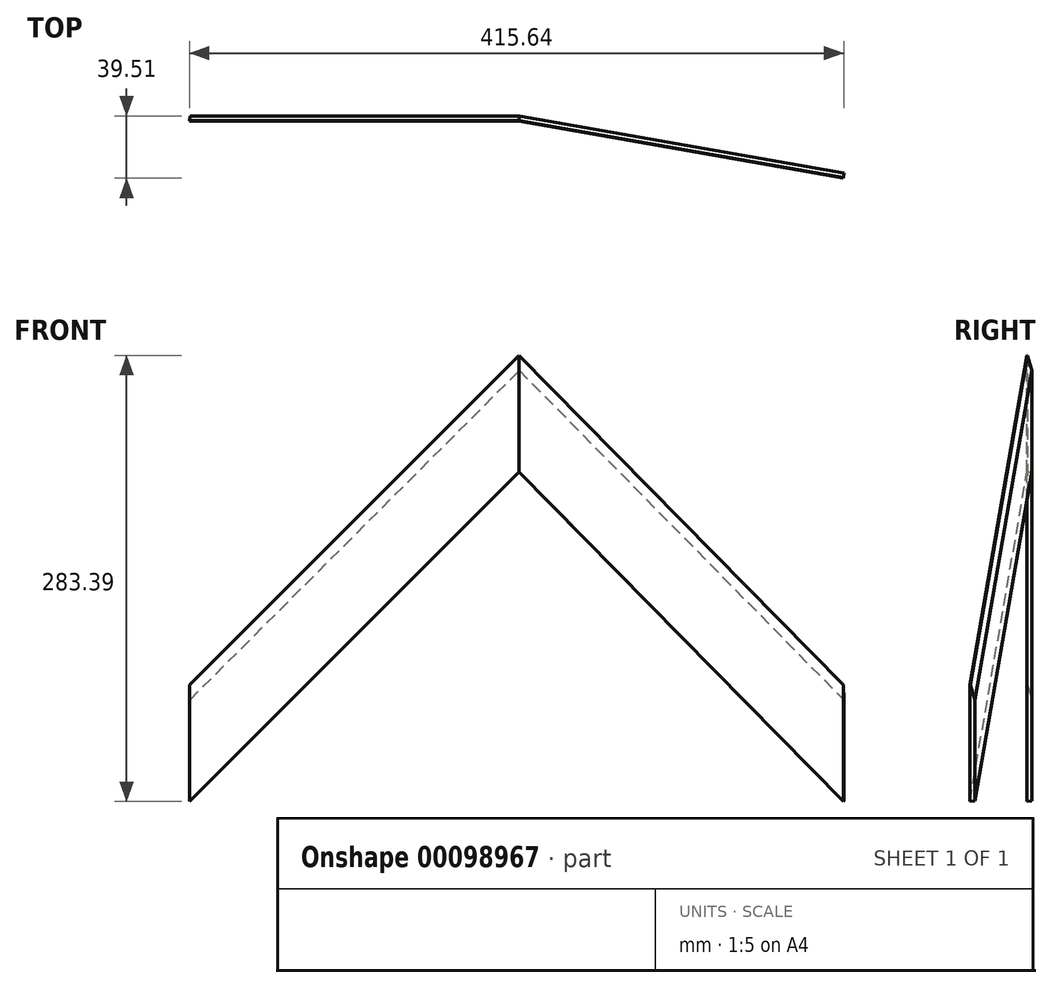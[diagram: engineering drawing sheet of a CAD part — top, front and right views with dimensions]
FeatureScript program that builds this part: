
annotation { "Feature Type Name" : "Feature", "Feature Type Description" : "" }
export const myFeature = defineFeature(function(context is Context, id is Id, definition is map)
    precondition{}
    {
        {
            var Q0;
            Q0=qCreatedBy(makeId("Front.planeOp"),FACE);
            var sketch = newSketch(context, id + "F0", { "sketchPlane" : qUnion([Q0])});
            skPoint(sketch, "E0.orphan", {"position": v(0, 0) * mm});
            skLineSegment(sketch, "E1", {"start": v(0, 0) * mm, "end": v(-215.9, 0) * mm, "construction": true});
            skLineSegment(sketch, "E2", {"start": v(-215.9, 0) * mm, "end": v(-215.9, -164.03) * mm, "construction": true});
            skLineSegment(sketch, "E3", {"start": v(-209.55, -283.64) * mm, "end": v(0, -74.09) * mm});
            skLineSegment(sketch, "E4", {"start": v(-209.55, -209.55) * mm, "end": v(0, 0) * mm});
            skLineSegment(sketch, "E5", {"start": v(0, 0) * mm, "end": v(0, -74.09) * mm});
            skPoint(sketch, "E6.orphan", {"position": v(-215.9, -215.9) * mm});
            skLineSegment(sketch, "E7.0", {"start": v(-209.55, -209.55) * mm, "end": v(-209.55, -283.64) * mm});
            skSolve(sketch);
        }
        {
            var Q0;
            Q0=makeQuery(id+"F0.imprint","IMPRINT",FACE,{"disambiguationData":[TD([[makeQuery(id+"F0.imprint","IMPRINT",EDGE,{"derivedFrom":sQuery(id+"F0.wireOp",EDGE,"E3")}),1.0]])]});
            extrude(context, id + "F1", {"entities" : qUnion([Q0]), "depth" : 3.17 * mm});
        }
        {
            var Q0;
            Q0=makeQuery(id+"F1.opExtrude","CAP_EDGE",EDGE,{"disambiguationData":[OSD([sQuery(id+"F0.wireOp",EDGE,"E5")])],"isStart":false});
            chamfer(context, id + "F2", {"entities" : qUnion([Q0]), "chamferType" : ChamferType.OFFSET_ANGLE, "width" : 3.17 * mm, "oppositeDirection" : false, "angle" : 5 * degree, "tangentPropagation" : true});
        }
        {
            var Q0;
            Q0=makeQuery(id+"F1.opExtrude","SWEPT_BODY",BODY,{"disambiguationData":[OSD([sQuery(id+"F0.wireOp",EDGE,"E3"),sQuery(id+"F0.wireOp",EDGE,"E4"),sQuery(id+"F0.wireOp",EDGE,"ONoessZQ-VDKj-vVyK-FP8X-JRhRMr7BJF2q"),sQuery(id+"F0.wireOp",EDGE,"E5")])]});
            var Q1;
            Q1=makeQuery(id+"F2.opChamfer","BLEND_FACE",FACE,{"disambiguationData":[OSD([sQuery(id+"F0.wireOp",EDGE,"E5")])]});
            mirror(context, id + "F3", {"operationType" : NewBodyOperationType.ADD, "entities" : qUnion([Q0]), "mirrorPlane" : qUnion([Q1])});
        }
        {
            var Q0;
            Q0=makeQuery(id+"F1.opExtrude","CAP_EDGE",EDGE,{"disambiguationData":[OSD([sQuery(id+"F0.wireOp",EDGE,"E4")])],"isStart":true});
            chamfer(context, id + "F4", {"entities" : qUnion([Q0]), "chamferType" : ChamferType.OFFSET_ANGLE, "width" : 7 * mm, "oppositeDirection" : false, "angle" : 22.5 * degree, "tangentPropagation" : true});
        }
        {
            var Q0;
            Q0=makeQuery(id+"F3.opPattern","COPY",EDGE,{"derivedFrom":makeQuery(id+"F1.opExtrude","CAP_EDGE",EDGE,{"disambiguationData":[OSD([sQuery(id+"F0.wireOp",EDGE,"E4")])],"isStart":true}),"instanceName":"1"});
            chamfer(context, id + "F5", {"entities" : qUnion([Q0]), "chamferType" : ChamferType.OFFSET_ANGLE, "width" : 7 * mm, "oppositeDirection" : true, "angle" : 22.5 * degree, "tangentPropagation" : true});
        }
        {
            var Q0;
            Q0=makeQuery(id+"F3.opPattern","COPY",EDGE,{"derivedFrom":makeQuery(id+"F1.opExtrude","CAP_EDGE",EDGE,{"disambiguationData":[OSD([sQuery(id+"F0.wireOp",EDGE,"E7.0")])],"isStart":true}),"instanceName":"1"});
            chamfer(context, id + "F6", {"entities" : qUnion([Q0]), "chamferType" : ChamferType.OFFSET_ANGLE, "width" : 3.17 * mm, "oppositeDirection" : true, "angle" : 5 * degree, "tangentPropagation" : true});
        }
        {
            var Q0;
            Q0=makeQuery(id+"F1.opExtrude","CAP_EDGE",EDGE,{"disambiguationData":[OSD([sQuery(id+"F0.wireOp",EDGE,"E7.0")])],"isStart":true});
            chamfer(context, id + "F7", {"entities" : qUnion([Q0]), "chamferType" : ChamferType.OFFSET_ANGLE, "width" : 3.17 * mm, "oppositeDirection" : false, "angle" : 5 * degree, "tangentPropagation" : true});
        }
    });
